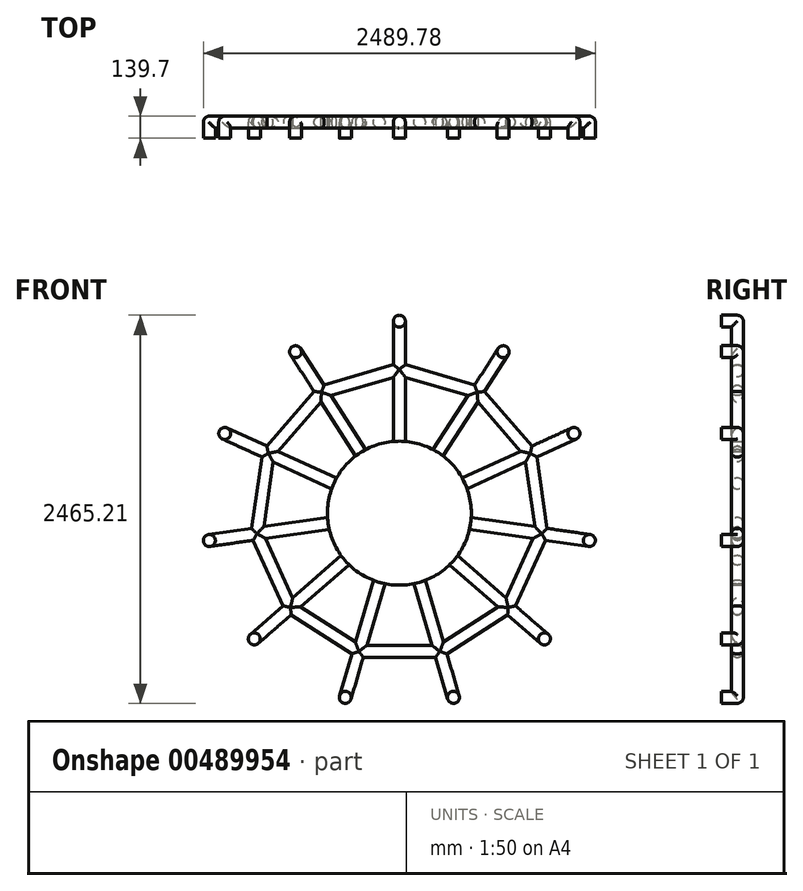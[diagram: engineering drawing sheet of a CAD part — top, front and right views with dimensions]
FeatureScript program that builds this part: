
annotation { "Feature Type Name" : "Feature", "Feature Type Description" : "" }
export const myFeature = defineFeature(function(context is Context, id is Id, definition is map)
    precondition{}
    {
        {
            var Q0;
            Q0=qCreatedBy(makeId("Front.planeOp"),FACE);
            var sketch = newSketch(context, id + "F0", { "sketchPlane" : qUnion([Q0])});
            skLineSegment(sketch, "E0", {"start": v(0, 0) * mm, "end": v(0, 1219.2) * mm});
            skCircle(sketch, "E1", {"center": v(0, 1219.2) * mm, "radius": 38.1 * mm});
            skCircle(sketch, "E2.1.0", {"center": v(-659.15, 1025.66) * mm, "radius": 38.1 * mm});
            skCircle(sketch, "E2.2.0", {"center": v(-1109.02, 506.47) * mm, "radius": 38.1 * mm});
            skCircle(sketch, "E2.3.0", {"center": v(-1206.8, -173.51) * mm, "radius": 38.1 * mm});
            skCircle(sketch, "E2.4.0", {"center": v(-921.4, -798.4) * mm, "radius": 38.1 * mm});
            skCircle(sketch, "E2.5.0", {"center": v(-343.49, -1169.81) * mm, "radius": 38.1 * mm});
            skCircle(sketch, "E2.6.0", {"center": v(343.49, -1169.81) * mm, "radius": 38.1 * mm});
            skCircle(sketch, "E2.7.0", {"center": v(921.4, -798.4) * mm, "radius": 38.1 * mm});
            skCircle(sketch, "E2.8.0", {"center": v(1206.8, -173.51) * mm, "radius": 38.1 * mm});
            skCircle(sketch, "E2.9.0", {"center": v(1109.02, 506.47) * mm, "radius": 38.1 * mm});
            skCircle(sketch, "E2.10.0", {"center": v(659.15, 1025.66) * mm, "radius": 38.1 * mm});
            skPoint(sketch, "E2.center", {"position": v(0, 0) * mm});
            skSolve(sketch);
        }
        {
            var Q0;
            Q0=makeQuery(id+"F0.imprint","IMPRINT",FACE,{"disambiguationData":[TD([[makeQuery(id+"F0.imprint","IMPRINT",EDGE,{"derivedFrom":sQuery(id+"F0.wireOp",EDGE,"E2.1.0")}),1.0]])]});
            var Q1;
            Q1=makeQuery(id+"F0.imprint","IMPRINT",FACE,{"disambiguationData":[TD([[makeQuery(id+"F0.imprint","IMPRINT",EDGE,{"derivedFrom":sQuery(id+"F0.wireOp",EDGE,"E1")}),1.0]])]});
            var Q2;
            Q2=makeQuery(id+"F0.imprint","IMPRINT",FACE,{"disambiguationData":[TD([[makeQuery(id+"F0.imprint","IMPRINT",EDGE,{"derivedFrom":sQuery(id+"F0.wireOp",EDGE,"E2.10.0")}),1.0]])]});
            var Q3;
            Q3=makeQuery(id+"F0.imprint","IMPRINT",FACE,{"disambiguationData":[TD([[makeQuery(id+"F0.imprint","IMPRINT",EDGE,{"derivedFrom":sQuery(id+"F0.wireOp",EDGE,"E2.9.0")}),1.0]])]});
            var Q4;
            Q4=makeQuery(id+"F0.imprint","IMPRINT",FACE,{"disambiguationData":[TD([[makeQuery(id+"F0.imprint","IMPRINT",EDGE,{"derivedFrom":sQuery(id+"F0.wireOp",EDGE,"E2.8.0")}),1.0]])]});
            var Q5;
            Q5=makeQuery(id+"F0.imprint","IMPRINT",FACE,{"disambiguationData":[TD([[makeQuery(id+"F0.imprint","IMPRINT",EDGE,{"derivedFrom":sQuery(id+"F0.wireOp",EDGE,"E2.7.0")}),1.0]])]});
            var Q6;
            Q6=makeQuery(id+"F0.imprint","IMPRINT",FACE,{"disambiguationData":[TD([[makeQuery(id+"F0.imprint","IMPRINT",EDGE,{"derivedFrom":sQuery(id+"F0.wireOp",EDGE,"E2.6.0")}),1.0]])]});
            var Q7;
            Q7=makeQuery(id+"F0.imprint","IMPRINT",FACE,{"disambiguationData":[TD([[makeQuery(id+"F0.imprint","IMPRINT",EDGE,{"derivedFrom":sQuery(id+"F0.wireOp",EDGE,"E2.5.0")}),1.0]])]});
            var Q8;
            Q8=makeQuery(id+"F0.imprint","IMPRINT",FACE,{"disambiguationData":[TD([[makeQuery(id+"F0.imprint","IMPRINT",EDGE,{"derivedFrom":sQuery(id+"F0.wireOp",EDGE,"E2.4.0")}),1.0]])]});
            var Q9;
            Q9=makeQuery(id+"F0.imprint","IMPRINT",FACE,{"disambiguationData":[TD([[makeQuery(id+"F0.imprint","IMPRINT",EDGE,{"derivedFrom":sQuery(id+"F0.wireOp",EDGE,"E2.3.0")}),1.0]])]});
            var Q10;
            Q10=makeQuery(id+"F0.imprint","IMPRINT",FACE,{"disambiguationData":[TD([[makeQuery(id+"F0.imprint","IMPRINT",EDGE,{"derivedFrom":sQuery(id+"F0.wireOp",EDGE,"E2.2.0")}),1.0]])]});
            extrude(context, id + "F1", {"entities" : qUnion([Q0, Q1, Q2, Q3, Q4, Q5, Q6, Q7, Q8, Q9, Q10]), "depth" : 101.6 * mm});
        }
        {
            var Q0;
            Q0=qCreatedBy(makeId("Front.planeOp"),FACE);
            var sketch = newSketch(context, id + "F2", { "sketchPlane" : qUnion([Q0])});
            skLineSegment(sketch, "E3", {"start": v(0, 0) * mm, "end": v(0, 1219.2) * mm});
            skLineSegment(sketch, "E4.0", {"start": v(38.1, 0) * mm, "end": v(38.1, 1219.2) * mm});
            skLineSegment(sketch, "E5.0", {"start": v(-38.1, 0) * mm, "end": v(-38.1, 1219.2) * mm});
            skLineSegment(sketch, "E6", {"start": v(38.1, 0) * mm, "end": v(-38.1, 0) * mm});
            skArc(sketch, "E7", {"start": v(38.1, 1219.2) * mm, "mid": v(0, 1257.3) * mm, "end": v(-38.1, 1219.2) * mm});
            skLineSegment(sketch, "E8", {"start": v(0, 1219.2) * mm, "end": v(0, 1257.3) * mm});
            skSolve(sketch);
        }
        {
            var Q0;
            {var subQ1=sQuery(id+"F2.wireOp",EDGE,"E3");Q0=makeQuery(id+"F2.imprint","IMPRINT",FACE,{"disambiguationData":[TD([[makeQuery(id+"F2.imprint","IMPRINT",EDGE,{"derivedFrom":subQ1}),-1.0]])]});}
            var Q1;
            Q1=sQuery(id+"F2.wireOp",EDGE,"E3");
            revolve(context, id + "F3", {"operationType" : NewBodyOperationType.ADD, "entities" : qUnion([Q0]), "axis" : qUnion([Q1]), "revolveType" : RevolveType.FULL});
        }
        {
            var Q0;
            Q0=qCreatedBy(makeId("Right.planeOp"),FACE);
            var sketch = newSketch(context, id + "F4", { "sketchPlane" : qUnion([Q0])});
            skLineSegment(sketch, "E9", {"start": v(0, 0) * mm, "end": v(153.65, 0) * mm});
            skSolve(sketch);
        }
        {
            var Q0;
            Q0=qCreatedBy(makeId("Front.planeOp"),FACE);
            var sketch = newSketch(context, id + "F5", { "sketchPlane" : qUnion([Q0])});
            skCircle(sketch, "E10", {"center": v(0, 0) * mm, "radius": 457.2 * mm});
            skSolve(sketch);
        }
        {
            var Q0;
            Q0=makeQuery(id+"F5.imprint","IMPRINT",FACE,{"disambiguationData":[TD([[makeQuery(id+"F5.imprint","IMPRINT",EDGE,{"derivedFrom":sQuery(id+"F5.wireOp",EDGE,"E10")}),1.0]])]});
            extrude(context, id + "F6", {"entities" : qUnion([Q0]), "operationType" : NewBodyOperationType.ADD, "endBound" : BoundingType.SYMMETRIC, "depth" : 76.2 * mm});
        }
        {
            var Q0;
            Q0=qCreatedBy(makeId("Front.planeOp"),FACE);
            var sketch = newSketch(context, id + "F7", { "sketchPlane" : qUnion([Q0])});
            skLineSegment(sketch, "E11", {"start": v(0, 0) * mm, "end": v(0, 914.4) * mm});
            skLineSegment(sketch, "E12.1.0", {"start": v(0, 0) * mm, "end": v(-494.36, 769.24) * mm});
            skLineSegment(sketch, "E12.2.0", {"start": v(0, 0) * mm, "end": v(-831.77, 379.86) * mm});
            skLineSegment(sketch, "E12.3.0", {"start": v(0, 0) * mm, "end": v(-905.1, -130.13) * mm});
            skLineSegment(sketch, "E12.4.0", {"start": v(0, 0) * mm, "end": v(-691.06, -598.8) * mm});
            skLineSegment(sketch, "E12.5.0", {"start": v(0, 0) * mm, "end": v(-257.62, -877.36) * mm});
            skLineSegment(sketch, "E12.6.0", {"start": v(0, 0) * mm, "end": v(257.62, -877.36) * mm});
            skLineSegment(sketch, "E12.7.0", {"start": v(0, 0) * mm, "end": v(691.06, -598.8) * mm});
            skLineSegment(sketch, "E12.8.0", {"start": v(0, 0) * mm, "end": v(905.1, -130.13) * mm});
            skLineSegment(sketch, "E12.9.0", {"start": v(0, 0) * mm, "end": v(831.77, 379.86) * mm});
            skLineSegment(sketch, "E12.10.0", {"start": v(0, 0) * mm, "end": v(494.36, 769.24) * mm});
            skPoint(sketch, "E12.center", {"position": v(0, 0) * mm});
            skLineSegment(sketch, "E13", {"start": v(-494.36, 769.24) * mm, "end": v(0, 914.4) * mm});
            skLineSegment(sketch, "E14.0", {"start": v(-505.1, 805.8) * mm, "end": v(-10.73, 950.96) * mm});
            skLineSegment(sketch, "E15.0", {"start": v(-483.63, 732.69) * mm, "end": v(10.73, 877.84) * mm});
            skLineSegment(sketch, "E16", {"start": v(-505.1, 805.8) * mm, "end": v(-494.36, 769.24) * mm});
            skLineSegment(sketch, "E17", {"start": v(-10.73, 950.96) * mm, "end": v(0, 914.4) * mm});
            skSolve(sketch);
        }
        {
            var Q0;
            Q0=makeQuery(id+"F7.imprint","IMPRINT",FACE,{"disambiguationData":[TD([[makeQuery(id+"F7.imprint","IMPRINT",EDGE,{"derivedFrom":sQuery(id+"F7.wireOp",EDGE,"E13")}),1.0]])]});
            var Q1;
            Q1=sQuery(id+"F7.wireOp",EDGE,"E13");
            revolve(context, id + "F8", {"operationType" : NewBodyOperationType.ADD, "entities" : qUnion([Q0]), "axis" : qUnion([Q1]), "revolveType" : RevolveType.FULL});
        }
        {
            var Q0;
            Q0=makeQuery(id+"F1.opExtrude","SWEPT_BODY",BODY,{"disambiguationData":[OSD([sQuery(id+"F0.wireOp",EDGE,"E1")])]});
            var Q1;
            Q1=sQuery(id+"F4.wireOp",EDGE,"E9");
            circularPattern(context, id + "F9", {"operationType" : NewBodyOperationType.ADD, "entities" : qUnion([Q0]), "axis" : qUnion([Q1]), "angle" : 360 * degree, "instanceCount" : 11, "equalSpace" : true});
        }
    });
